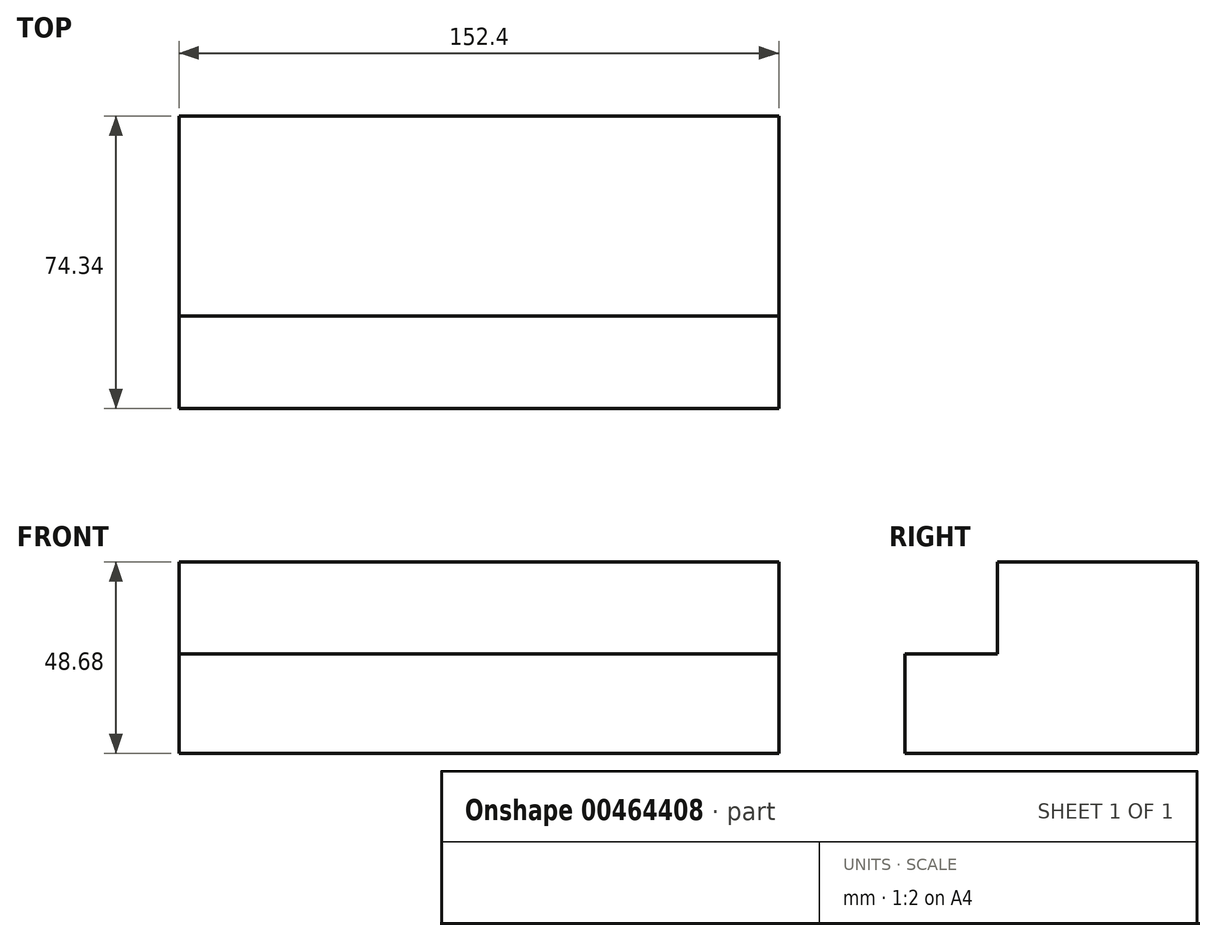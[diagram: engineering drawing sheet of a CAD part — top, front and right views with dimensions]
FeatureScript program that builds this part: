
annotation { "Feature Type Name" : "Feature", "Feature Type Description" : "" }
export const myFeature = defineFeature(function(context is Context, id is Id, definition is map)
    precondition{}
    {
        {
            var Q0;
            Q0=qCreatedBy(makeId("Right.planeOp"),FACE);
            var sketch = newSketch(context, id + "F0", { "sketchPlane" : qUnion([Q0])});
            skLineSegment(sketch, "E0", {"start": v(75.53, 61.97) * mm, "end": v(24.73, 61.97) * mm});
            skLineSegment(sketch, "E1", {"start": v(24.73, 61.97) * mm, "end": v(24.73, 38.6) * mm});
            skLineSegment(sketch, "E2", {"start": v(24.73, 38.6) * mm, "end": v(1.19, 38.6) * mm});
            skLineSegment(sketch, "E3", {"start": v(1.19, 38.6) * mm, "end": v(1.19, 13.3) * mm});
            skLineSegment(sketch, "E4", {"start": v(1.19, 13.3) * mm, "end": v(75.53, 13.3) * mm});
            skLineSegment(sketch, "E5", {"start": v(75.53, 13.3) * mm, "end": v(75.53, 61.97) * mm});
            skSolve(sketch);
        }
        {
            var Q0;
            Q0=makeQuery(id+"F0.imprint","IMPRINT",FACE,{"disambiguationData":[TD([[makeQuery(id+"F0.imprint","IMPRINT",EDGE,{"derivedFrom":sQuery(id+"F0.wireOp",EDGE,"E0")}),1.0]])]});
            extrude(context, id + "F1", {"entities" : qUnion([Q0]), "depth" : 152.4 * mm});
        }
    });
